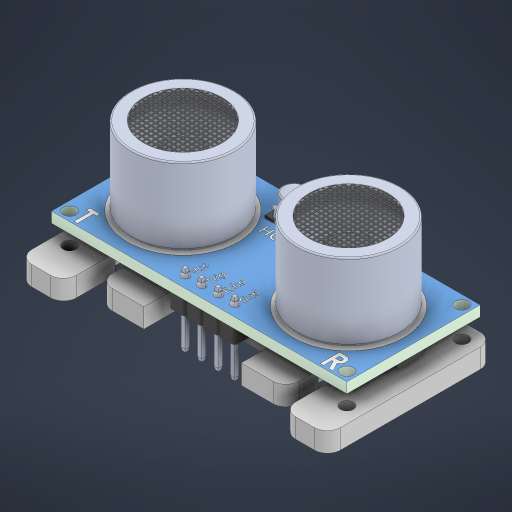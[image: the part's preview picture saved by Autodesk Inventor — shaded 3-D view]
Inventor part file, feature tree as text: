
AUTODESK INVENTOR PART (.ipt)
format: ipt  version: 2023 (Build 270158000, 158)  size: 8,420,352 bytes
history: native  units: mm
features: other x46, sketch x2, plane x1, extrude x1, fillet x1, projected_geometry x1
ambient origin geometry x8: Origin, YZ Plane, XZ Plane, XY Plane, X Axis, Y Axis, Z Axis, Center Point
bodies: Solid1 (feature_tree), Solid2 (feature_tree), Solid3 (feature_tree), Solid4 (feature_tree), Solid5 (feature_tree), Solid6 (feature_tree), Solid7 (feature_tree), Solid8 (feature_tree), Solid9 (feature_tree), Solid10 (feature_tree), Solid11 (feature_tree), Solid12 (feature_tree), Solid13 (feature_tree), Solid14 (feature_tree), Solid15 (feature_tree), Solid16 (feature_tree), Solid17 (feature_tree), Solid18 (feature_tree), Solid19 (feature_tree), Solid20 (feature_tree), Solid21 (feature_tree), Solid22 (feature_tree), Solid23 (feature_tree), Solid24 (feature_tree), Solid25 (feature_tree), Solid26 (feature_tree), Solid27 (feature_tree), Solid28 (feature_tree), Solid29 (feature_tree), Solid30 (feature_tree), Solid31 (feature_tree), Solid32 (feature_tree), Solid33 (feature_tree), Solid34 (feature_tree), Solid35 (feature_tree), Solid36 (feature_tree), Solid37 (feature_tree), Solid38 (feature_tree), Solid39 (feature_tree), Solid40 (feature_tree), Solid41 (feature_tree), Solid42 (feature_tree), Solid43 (feature_tree), Solid44 (feature_tree), Solid45 (feature_tree)
feature tree (52):
  other  "HC-SR04.iam"
  other  "HC-SR04board.ipt:1"
  other  "solder.ipt:1"
  other  "solder.ipt:2"
  other  "solder.ipt:3"
  other  "solder.ipt:4"
  other  "Emitter.ipt:1"
  other  "Emitter.ipt:2"
  other  "CrystalOscillator.ipt:1"
  other  "solder.ipt:5"
  other  "solder.ipt:6"
  other  "smdChip14pin.ipt:1"
  other  "smdChip14pin.ipt:2"
  other  "smdChip16pin.ipt:1"
  other  "smdceramiccapacitor.ipt:1"
  other  "smdceramiccapacitor.ipt:2"
  other  "smdceramiccapacitor.ipt:3"
  other  "smdceramiccapacitor.ipt:4"
  other  "smdceramiccapacitor.ipt:5"
  other  "smdceramiccapacitor.ipt:6"
  other  "smdceramiccapacitor.ipt:7"
  other  "smdResistor753.ipt:1"
  other  "smdResistor753.ipt:2"
  other  "smdResistor753.ipt:3"
  other  "smdResistor392.ipt:1"
  other  "smdResistor103.ipt:1"
  other  "smdResistor124.ipt:1"
  other  "smdResistor103.ipt:2"
  other  "smdResistor103.ipt:3"
  other  "smdResistor335.ipt:1"
  other  "smdResistor102.ipt:1"
  other  "smdResistor103.ipt:4"
  other  "smdResistor563.ipt:1"
  other  "smdResistor103.ipt:5"
  other  "smdResistor622.ipt:1"
  other  "smdResistor124.ipt:2"
  other  "smdResistor412.ipt:1"
  other  "smdResistor103.ipt:6"
  other  "solder.ipt:7"
  other  "solder.ipt:8"
  other  "solder.ipt:9"
  other  "solder.ipt:10"
  other  "headerMale.ipt:1"
  other  "headerMale.ipt:2"
  other  "headerMale.ipt:3"
  other  "headerMale.ipt:4"
  plane  "Work Plane1"
  extrude  "Extrusion1"  Depth=10.0mm
  sketch  "Sketch2"  dims[d3=15.0mm d4=1.0mm d5=6.0mm d6=2.5mm d7=10.0mm d8=5.1mm d9=2.1mm d10=3.0mm d11=0.0mm d12=3.0mm d13=2.0mm]
  fillet  "Fillet1"  Radius=5.0mm
  sketch  "Sketch1"  dims[d0=10.0mm d1=3.0mm d2=5.0mm]
  projected_geometry  "Projected Loop1"
